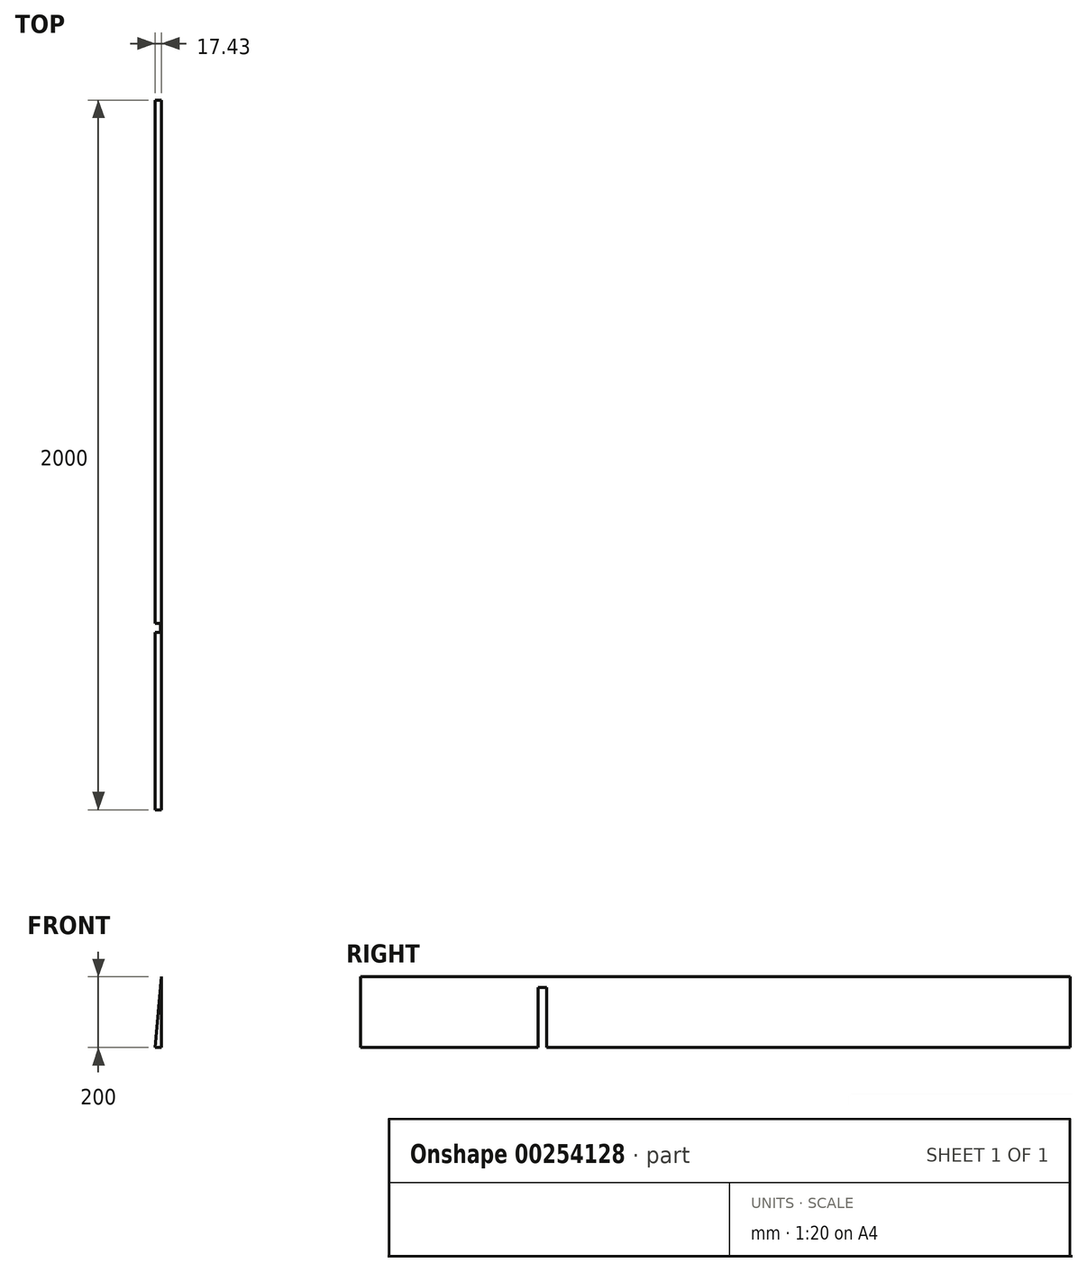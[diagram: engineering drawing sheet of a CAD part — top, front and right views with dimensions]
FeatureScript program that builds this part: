
annotation { "Feature Type Name" : "Feature", "Feature Type Description" : "" }
export const myFeature = defineFeature(function(context is Context, id is Id, definition is map)
    precondition{}
    {
        {
            var Q0;
            Q0=qCreatedBy(makeId("Front.planeOp"),FACE);
            var sketch = newSketch(context, id + "F0", { "sketchPlane" : qUnion([Q0])});
            skCircle(sketch, "E0", {"center": v(0, 0) * mm, "radius": 200 * mm});
            skSolve(sketch);
        }
        {
            var Q0;
            Q0 = qSketchRegion(id + "F0", true);
            extrude(context, id + "F1", {"entities" : qUnion([Q0]), "depth" : 2000 * mm});
        }
        {
            var Q0;
            Q0=makeQuery(id+"F1.opExtrude","CAP_FACE",FACE,{"disambiguationData":[OSD([sQuery(id+"F0.wireOp",EDGE,"E0")])],"isStart":false});
            cPlane(context, id + "F2", {"entities" : qUnion([Q0]), "cplaneType" : CPlaneType.OFFSET, "offset" : 500 * mm, "oppositeDirection" : true, "width" : 150 * mm, "height" : 150 * mm});
        }
        {
            var Q0;
            Q0=qCreatedBy(id+"F2.planeOp",FACE);
            var sketch = newSketch(context, id + "F3", { "sketchPlane" : qUnion([Q0])});
            skLineSegment(sketch, "E1.bottom", {"start": v(150, -30) * mm, "end": v(-150, -30) * mm});
            skLineSegment(sketch, "E1.top", {"start": v(150, 30) * mm, "end": v(-150, 30) * mm});
            skLineSegment(sketch, "E1.left", {"start": v(150, -30) * mm, "end": v(150, 30) * mm});
            skLineSegment(sketch, "E1.right", {"start": v(-150, -30) * mm, "end": v(-150, 30) * mm});
            skPoint(sketch, "E1.middle", {"position": v(0, 0) * mm});
            skCircle(sketch, "E2", {"center": v(0, 0) * mm, "radius": 377.25 * mm});
            skSolve(sketch);
        }
        {
            var Q0;
            Q0=makeQuery(id+"F3.imprint","IMPRINT",FACE,{"disambiguationData":[TD([[makeQuery(id+"F3.imprint","IMPRINT",EDGE,{"derivedFrom":sQuery(id+"F3.wireOp",EDGE,"E1.bottom")}),1.0]])]});
            extrude(context, id + "F4", {"entities" : qUnion([Q0]), "operationType" : NewBodyOperationType.REMOVE, "oppositeDirection" : true, "depth" : 25 * mm});
        }
        {
            var Q0;
            Q0=makeQuery(id+"F1.opExtrude","CAP_FACE",FACE,{"disambiguationData":[OSD([sQuery(id+"F0.wireOp",EDGE,"E0")])],"isStart":false});
            var sketch = newSketch(context, id + "F5", { "sketchPlane" : qUnion([Q0])});
            skLineSegment(sketch, "E3", {"start": v(0, 0) * mm, "end": v(0, -200) * mm});
            skLineSegment(sketch, "E4", {"start": v(0, 0) * mm, "end": v(-17.43, -199.24) * mm});
            skSolve(sketch);
        }
        {
            var Q0;
            {var subQ0=sQuery(id+"F5.wireOp",EDGE,"E3");Q0=makeQuery(id+"F5.imprint","IMPRINT",FACE,{"disambiguationData":[TD([[makeQuery(id+"F5.imprint","IMPRINT",EDGE,{"derivedFrom":subQ0}),-1.0]])]});}
            extrude(context, id + "F6", {"entities" : qUnion([Q0]), "operationType" : NewBodyOperationType.INTERSECT, "oppositeDirection" : true, "depth" : 2000 * mm});
        }
    });
